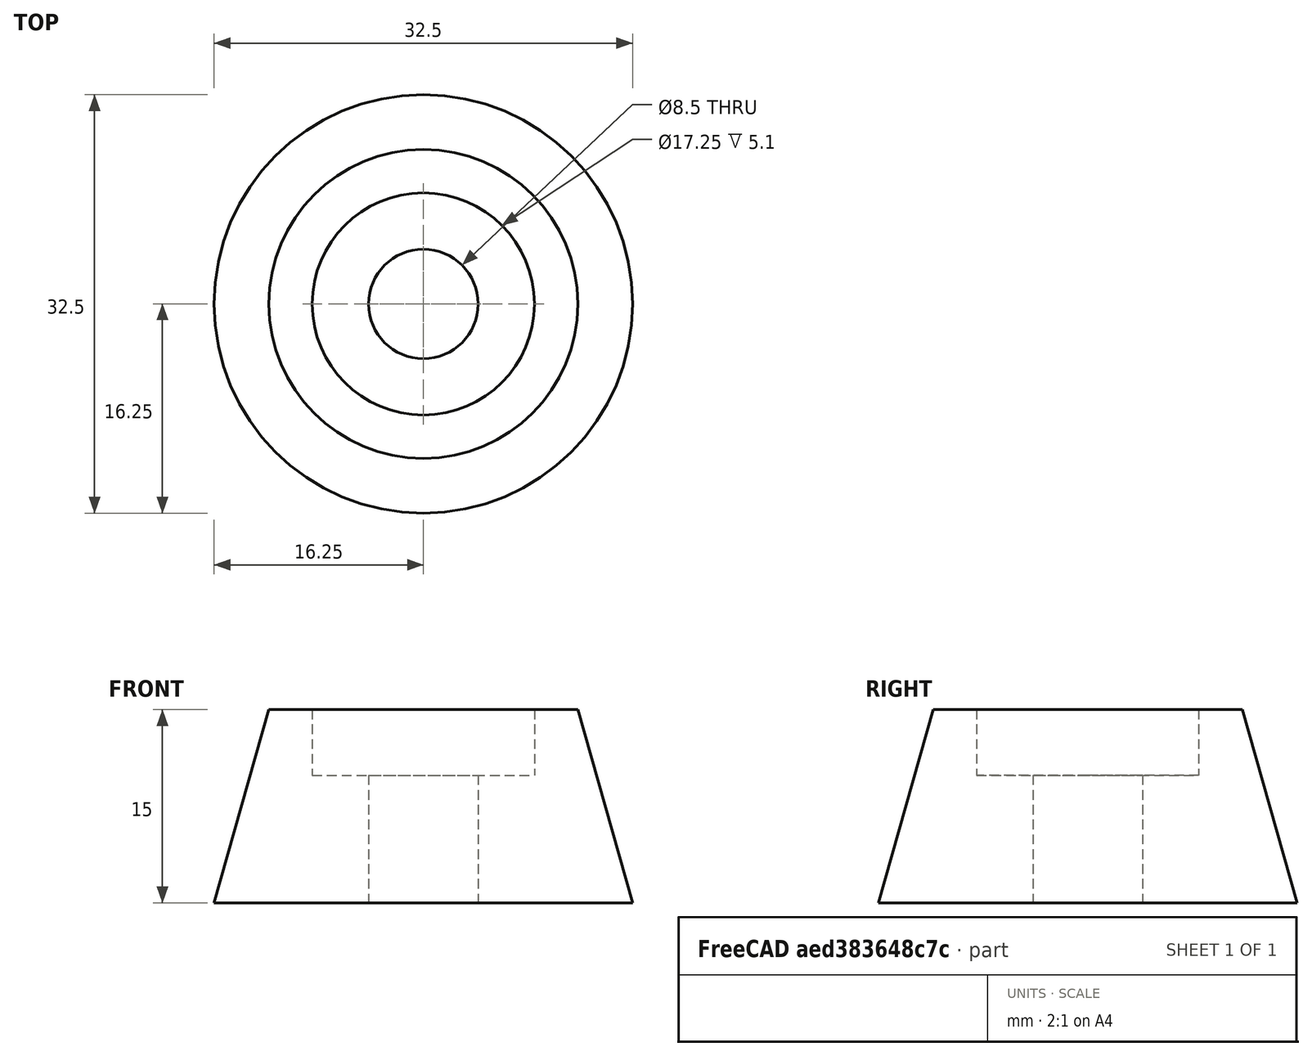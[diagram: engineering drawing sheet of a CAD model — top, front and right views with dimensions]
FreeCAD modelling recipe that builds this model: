
FCSTD DOCUMENT  (FreeCAD 0.18R)
Label: foot-mount
License: All rights reserved
LicenseURL: http://en.wikipedia.org/wiki/All_rights_reserved
objects: Sketcher::SketchObject×1, PartDesign::Revolution×1, PartDesign::Body×1
note: 4 computed .brp shape members not serialized (recipe doc carries the construction recipe); baked Part::Feature solids carry a one-line shape summary decoded from their .brp

FEATURE [Sketcher::SketchObject] Sketch001
  MapMode = 5
  Placement = pos=(0,0,0) rot=(1,0,0;1.5708rad)
  Support = -> [XZ_Plane]
  sketch-geometry (6):
    g0: LineSegment StartX=-8.625 StartY=9.9 StartZ=0 EndX=-4.25 EndY=9.9 EndZ=0
    g1: LineSegment StartX=-4.25 StartY=9.9 StartZ=0 EndX=-4.25 EndY=0 EndZ=0
    g2: LineSegment StartX=-16.25 StartY=0 StartZ=0 EndX=-4.25 EndY=0 EndZ=0
    g3: LineSegment StartX=-16.25 StartY=0 StartZ=0 EndX=-12 EndY=15 EndZ=0
    g4: LineSegment StartX=-12 StartY=15 StartZ=0 EndX=-8.625 EndY=15 EndZ=0
    g5: LineSegment StartX=-8.625 StartY=15 StartZ=0 EndX=-8.625 EndY=9.9 EndZ=0
  constraints (18):
    c: Horizontal(g0)
    c: Vertical(g1)
    c: PointOnObject(g2,g-1)
    c: PointOnObject(g2,g-1)
    c: Coincident(g1,g2)
    c: Coincident(g0,g1)
    c: DistanceX(g0,g-1) = 4.25
    c: DistanceX(g2,g2) = 12
    c: Coincident(g3,g2)
    c: Horizontal(g4)
    c: Vertical(g5)
    c: Coincident(g4,g3)
    c: Coincident(g4,g5)
    c: DistanceX(g5,g-1) = 8.625
    c: Coincident(g5,g0)
    c: DistanceX(g3,g-1) = 12
    c: DistanceY(g-1,g4) = 15
    c: DistanceY(g0,g4) = 5.1
FEATURE [PartDesign::Revolution] Revolution  label="Revolution001"
  Angle = 360
  Axis = (0,-2e-16,1)
  Base = (0,0,0)
  Placement = pos=(0,0,0) rot=(1,0,0;1.5708rad)
  Profile = -> Sketch001
  ReferenceAxis = -> Sketch001 [V_Axis]
FEATURE [PartDesign::Body] Body001  label="foot-mount"
  Group = -> [Sketch001,Revolution]
  Origin = -> Origin
  Tip = -> Revolution
